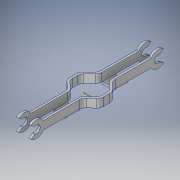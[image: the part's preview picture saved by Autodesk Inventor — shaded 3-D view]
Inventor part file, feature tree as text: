
AUTODESK INVENTOR PART (.ipt)
format: ipt  version: 2018 (Build 220112000, 112)  size: 261,120 bytes
history: native  units: in
note: dims shown in document units (in); Inventor stores cm internally (conversion verified against a paired STEP export)
features: extrude x6, sketch x6, fillet x2, mirror x2, plane x1
ambient origin geometry x8: Origin, YZ Plane, XZ Plane, XY Plane, X Axis, Y Axis, Z Axis, Center Point
bodies: Solid1 (feature_tree)
feature tree (17):
  extrude  "Extrusion1"  Depth=0.12in
  extrude  "Extrusion3"  Depth=0.025in TaperAngle=0.0deg
  fillet  "Fillet4"  Radius=0.025in
  extrude  "Extrusion6"  Depth=0.1in
  extrude  "Extrusion8"  Depth=0.06in TaperAngle=0.0deg
  fillet  "Fillet6"  Radius=0.06in
  extrude  "Extrusion10"  Depth=0.14in TaperAngle=0.0deg
  extrude  "Extrusion11"  Depth=0.14in
  plane  "Work Plane3"
  mirror  "Mirror2"
  mirror  "Mirror3"
  sketch  "Sketch1"  dims[d14=0.08in d15=0.0in d33=0.12in]
  sketch  "Sketch3"  dims[d34=0.12in d35=0.025in d36=0.0in d37=0.025in]
  sketch  "Sketch6"  dims[d45=1.0in d46=0.0in d50=0.1in]
  sketch  "Sketch9"  dims[d51=0.3in d52=1.0in d53=0.0in d65=0.06in]
  sketch  "Sketch11"  dims[d66=0.157in d69=0.14in d70=0.0in]
  sketch  "Sketch12"  dims[d71=0.14in d72=0.0in d73=0.174in d74=0.074in d75=0.9963in d76=0.9963in]
